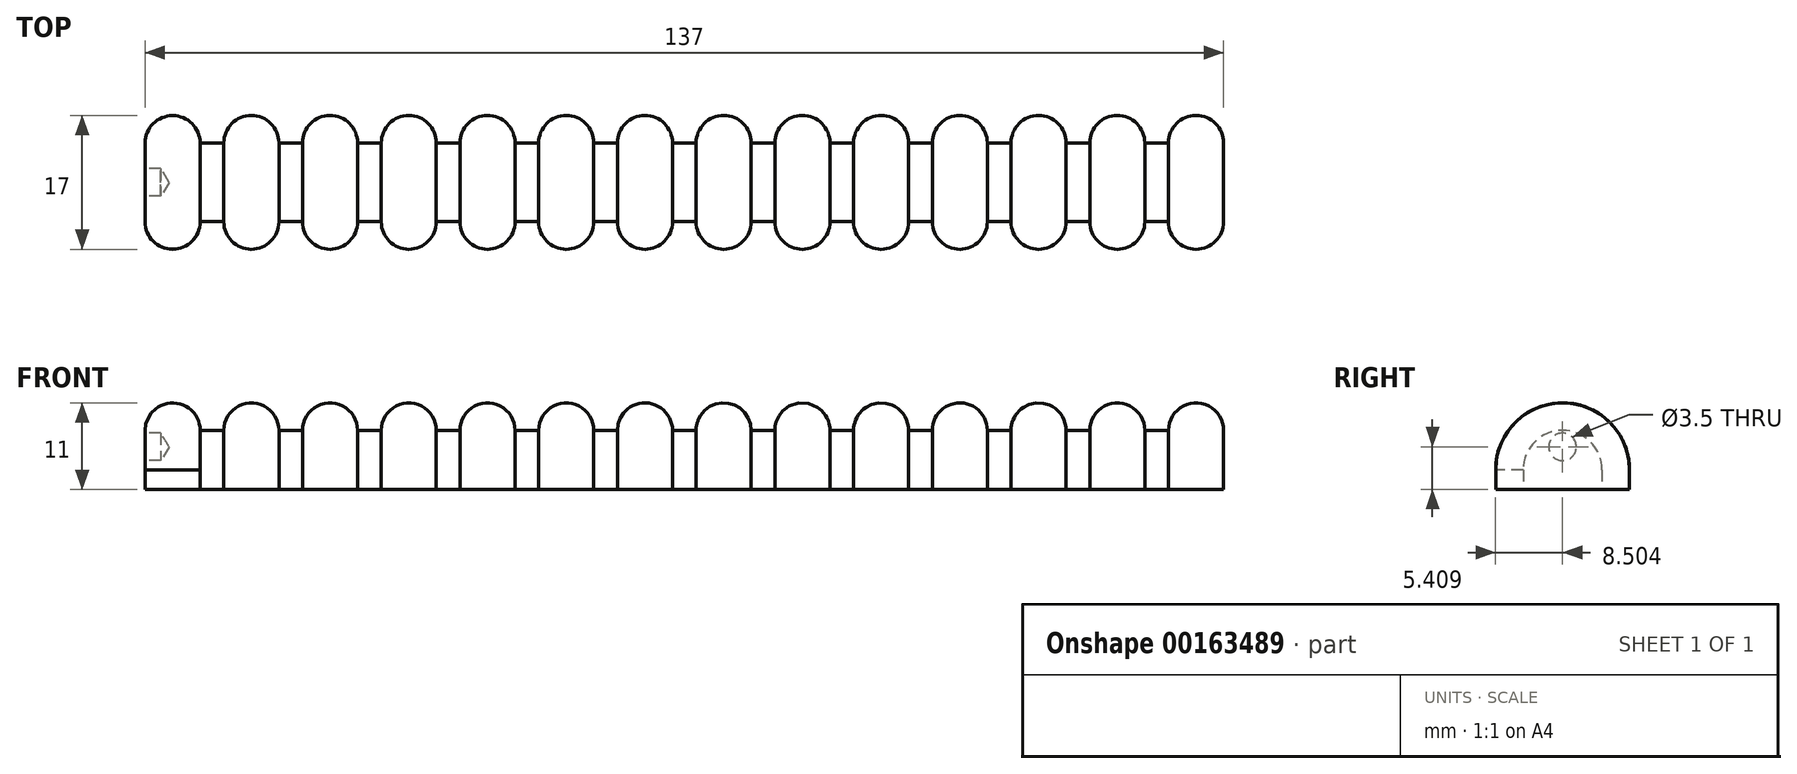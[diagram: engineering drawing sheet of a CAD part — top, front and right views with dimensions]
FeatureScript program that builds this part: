
annotation { "Feature Type Name" : "Feature", "Feature Type Description" : "" }
export const myFeature = defineFeature(function(context is Context, id is Id, definition is map)
    precondition{}
    {
        {
            var Q0;
            Q0=qCreatedBy(makeId("Top.planeOp"),FACE);
            var sketch = newSketch(context, id + "F0", { "sketchPlane" : qUnion([Q0])});
            skLineSegment(sketch, "E0", {"start": v(9.65, 1.22) * mm, "end": v(9.65, 0.22) * mm});
            skLineSegment(sketch, "E1", {"start": v(9.65, 0.22) * mm, "end": v(14.65, 0.22) * mm});
            skLineSegment(sketch, "E2", {"start": v(14.65, 0.22) * mm, "end": v(14.65, 1.22) * mm});
            skLineSegment(sketch, "E3", {"start": v(19.65, 1.22) * mm, "end": v(19.65, 0.22) * mm});
            skLineSegment(sketch, "E4", {"start": v(19.65, 0.22) * mm, "end": v(24.65, 0.22) * mm});
            skLineSegment(sketch, "E5", {"start": v(24.65, 0.22) * mm, "end": v(24.65, 1.22) * mm});
            skLineSegment(sketch, "E6", {"start": v(29.65, 1.22) * mm, "end": v(29.65, 0.22) * mm});
            skLineSegment(sketch, "E7", {"start": v(29.65, 0.22) * mm, "end": v(34.65, 0.22) * mm});
            skLineSegment(sketch, "E8", {"start": v(34.65, 0.22) * mm, "end": v(34.65, 1.22) * mm});
            skLineSegment(sketch, "E9", {"start": v(39.65, 1.22) * mm, "end": v(39.65, 0.22) * mm});
            skLineSegment(sketch, "E10", {"start": v(39.65, 0.22) * mm, "end": v(44.65, 0.22) * mm});
            skLineSegment(sketch, "E11", {"start": v(44.65, 0.22) * mm, "end": v(44.65, 1.22) * mm});
            skLineSegment(sketch, "E12", {"start": v(49.65, 1.22) * mm, "end": v(49.65, 0.22) * mm});
            skLineSegment(sketch, "E13", {"start": v(49.65, 0.22) * mm, "end": v(54.65, 0.22) * mm});
            skLineSegment(sketch, "E14", {"start": v(54.65, 0.22) * mm, "end": v(54.65, 1.22) * mm});
            skLineSegment(sketch, "E15", {"start": v(59.65, 1.22) * mm, "end": v(59.65, 0.22) * mm});
            skLineSegment(sketch, "E16", {"start": v(59.65, 0.22) * mm, "end": v(64.65, 0.22) * mm});
            skLineSegment(sketch, "E17", {"start": v(64.65, 0.22) * mm, "end": v(64.65, 1.22) * mm});
            skLineSegment(sketch, "E18", {"start": v(69.65, 1.22) * mm, "end": v(69.65, 0.22) * mm});
            skLineSegment(sketch, "E19", {"start": v(69.65, 0.22) * mm, "end": v(74.65, 0.22) * mm});
            skLineSegment(sketch, "E20", {"start": v(74.65, 0.22) * mm, "end": v(74.65, 1.22) * mm});
            skLineSegment(sketch, "E21", {"start": v(79.65, 1.22) * mm, "end": v(79.65, 0.22) * mm});
            skLineSegment(sketch, "E22", {"start": v(79.65, 0.22) * mm, "end": v(84.65, 0.22) * mm});
            skLineSegment(sketch, "E23", {"start": v(84.65, 0.22) * mm, "end": v(84.65, 1.22) * mm});
            skLineSegment(sketch, "E24", {"start": v(89.65, 1.22) * mm, "end": v(89.65, 0.22) * mm});
            skLineSegment(sketch, "E25", {"start": v(89.65, 0.22) * mm, "end": v(94.65, 0.22) * mm});
            skLineSegment(sketch, "E26", {"start": v(94.65, 0.22) * mm, "end": v(94.65, 1.22) * mm});
            skLineSegment(sketch, "E27", {"start": v(99.65, 1.22) * mm, "end": v(99.65, 0.22) * mm});
            skLineSegment(sketch, "E28", {"start": v(99.65, 0.22) * mm, "end": v(104.65, 0.22) * mm});
            skLineSegment(sketch, "E29", {"start": v(104.65, 0.22) * mm, "end": v(104.65, 1.22) * mm});
            skLineSegment(sketch, "E30", {"start": v(109.65, 1.22) * mm, "end": v(109.65, 0.22) * mm});
            skLineSegment(sketch, "E31", {"start": v(109.65, 0.22) * mm, "end": v(114.65, 0.22) * mm});
            skLineSegment(sketch, "E32", {"start": v(114.65, 0.22) * mm, "end": v(114.65, 1.22) * mm});
            skLineSegment(sketch, "E33", {"start": v(119.65, 1.22) * mm, "end": v(119.65, 0.22) * mm});
            skLineSegment(sketch, "E34", {"start": v(119.65, 0.22) * mm, "end": v(124.65, 0.22) * mm});
            skLineSegment(sketch, "E35", {"start": v(124.65, 0.22) * mm, "end": v(124.65, 1.22) * mm});
            skLineSegment(sketch, "E36", {"start": v(124.65, 1.22) * mm, "end": v(127.15, 1.22) * mm});
            skLineSegment(sketch, "E37", {"start": v(129.65, 1.22) * mm, "end": v(129.65, 0.22) * mm});
            skLineSegment(sketch, "E38", {"start": v(129.65, 0.22) * mm, "end": v(134.65, 0.22) * mm});
            skLineSegment(sketch, "E39", {"start": v(134.65, 0.22) * mm, "end": v(134.65, 1.22) * mm});
            skLineSegment(sketch, "E40", {"start": v(139.65, 1.22) * mm, "end": v(139.65, -8.78) * mm});
            skLineSegment(sketch, "E41", {"start": v(134.65, -8.78) * mm, "end": v(134.65, -7.78) * mm});
            skLineSegment(sketch, "E42", {"start": v(134.65, -7.78) * mm, "end": v(129.65, -7.78) * mm});
            skLineSegment(sketch, "E43", {"start": v(129.65, -7.78) * mm, "end": v(129.65, -8.78) * mm});
            skLineSegment(sketch, "E44", {"start": v(124.65, -8.78) * mm, "end": v(124.65, -7.78) * mm});
            skLineSegment(sketch, "E45", {"start": v(124.65, -7.78) * mm, "end": v(119.65, -7.78) * mm});
            skLineSegment(sketch, "E46", {"start": v(119.65, -7.78) * mm, "end": v(119.65, -8.78) * mm});
            skLineSegment(sketch, "E47", {"start": v(114.65, -8.78) * mm, "end": v(114.65, -7.78) * mm});
            skLineSegment(sketch, "E48", {"start": v(114.65, -7.78) * mm, "end": v(109.65, -7.78) * mm});
            skLineSegment(sketch, "E49", {"start": v(109.65, -7.78) * mm, "end": v(109.65, -8.78) * mm});
            skLineSegment(sketch, "E50", {"start": v(104.65, -8.78) * mm, "end": v(104.65, -7.78) * mm});
            skLineSegment(sketch, "E51", {"start": v(69.65, -7.78) * mm, "end": v(69.65, -8.78) * mm});
            skLineSegment(sketch, "E52", {"start": v(64.65, -8.78) * mm, "end": v(64.65, -7.78) * mm});
            skLineSegment(sketch, "E53", {"start": v(64.65, -7.78) * mm, "end": v(59.65, -7.78) * mm});
            skLineSegment(sketch, "E54", {"start": v(59.65, -7.78) * mm, "end": v(59.65, -8.78) * mm});
            skLineSegment(sketch, "E55", {"start": v(54.65, -8.78) * mm, "end": v(54.65, -7.78) * mm});
            skLineSegment(sketch, "E56", {"start": v(54.65, -7.78) * mm, "end": v(49.65, -7.78) * mm});
            skLineSegment(sketch, "E57", {"start": v(49.65, -7.78) * mm, "end": v(49.65, -8.78) * mm});
            skLineSegment(sketch, "E58", {"start": v(44.65, -8.78) * mm, "end": v(44.65, -7.78) * mm});
            skLineSegment(sketch, "E59", {"start": v(44.65, -7.78) * mm, "end": v(39.65, -7.78) * mm});
            skLineSegment(sketch, "E60", {"start": v(39.65, -7.78) * mm, "end": v(39.65, -8.78) * mm});
            skLineSegment(sketch, "E61", {"start": v(34.65, -8.78) * mm, "end": v(34.65, -7.78) * mm});
            skLineSegment(sketch, "E62", {"start": v(34.65, -7.78) * mm, "end": v(29.65, -7.78) * mm});
            skLineSegment(sketch, "E63", {"start": v(29.65, -7.78) * mm, "end": v(29.65, -8.78) * mm});
            skLineSegment(sketch, "E64", {"start": v(24.65, -8.78) * mm, "end": v(24.65, -7.78) * mm});
            skLineSegment(sketch, "E65", {"start": v(24.65, -7.78) * mm, "end": v(19.65, -7.78) * mm});
            skLineSegment(sketch, "E66", {"start": v(19.65, -7.78) * mm, "end": v(19.65, -8.78) * mm});
            skLineSegment(sketch, "E67", {"start": v(14.65, -8.78) * mm, "end": v(14.65, -7.78) * mm});
            skLineSegment(sketch, "E68", {"start": v(14.65, -7.78) * mm, "end": v(9.65, -7.78) * mm});
            skLineSegment(sketch, "E69", {"start": v(9.65, -7.78) * mm, "end": v(9.65, -8.78) * mm});
            skLineSegment(sketch, "E70", {"start": v(4.65, -8.78) * mm, "end": v(4.65, 1.22) * mm});
            skArc(sketch, "E71", {"start": v(4.65, 1.22) * mm, "mid": v(7.15, 3.7) * mm, "end": v(9.65, 1.22) * mm});
            skArc(sketch, "E72", {"start": v(14.65, 1.22) * mm, "mid": v(17.15, 3.72) * mm, "end": v(19.65, 1.22) * mm});
            skArc(sketch, "E73", {"start": v(4.65, -8.78) * mm, "mid": v(7.15, -11.28) * mm, "end": v(9.65, -8.78) * mm});
            skArc(sketch, "E74", {"start": v(14.65, -8.78) * mm, "mid": v(17.15, -11.28) * mm, "end": v(19.65, -8.78) * mm});
            skLineSegment(sketch, "E75", {"start": v(79.65, -7.78) * mm, "end": v(79.65, -8.78) * mm});
            skLineSegment(sketch, "E76", {"start": v(74.65, -8.78) * mm, "end": v(74.65, -7.78) * mm});
            skLineSegment(sketch, "E77", {"start": v(74.65, -7.78) * mm, "end": v(69.65, -7.78) * mm});
            skArc(sketch, "E78", {"start": v(24.65, -8.78) * mm, "mid": v(27.15, -11.28) * mm, "end": v(29.65, -8.78) * mm});
            skArc(sketch, "E79", {"start": v(24.65, 1.22) * mm, "mid": v(27.15, 3.72) * mm, "end": v(29.65, 1.22) * mm});
            skArc(sketch, "E80", {"start": v(34.65, 1.22) * mm, "mid": v(37.15, 3.72) * mm, "end": v(39.65, 1.22) * mm});
            skArc(sketch, "E81", {"start": v(34.65, -8.78) * mm, "mid": v(37.15, -11.28) * mm, "end": v(39.65, -8.78) * mm});
            skArc(sketch, "E82", {"start": v(44.65, -8.78) * mm, "mid": v(47.15, -11.28) * mm, "end": v(49.65, -8.78) * mm});
            skArc(sketch, "E83", {"start": v(44.65, 1.22) * mm, "mid": v(47.15, 3.72) * mm, "end": v(49.65, 1.22) * mm});
            skArc(sketch, "E84", {"start": v(54.65, 1.22) * mm, "mid": v(57.15, 3.72) * mm, "end": v(59.65, 1.22) * mm});
            skArc(sketch, "E85", {"start": v(54.65, -8.78) * mm, "mid": v(57.15, -11.28) * mm, "end": v(59.65, -8.78) * mm});
            skArc(sketch, "E86", {"start": v(64.65, -8.78) * mm, "mid": v(67.15, -11.28) * mm, "end": v(69.65, -8.78) * mm});
            skArc(sketch, "E87", {"start": v(64.65, 1.22) * mm, "mid": v(67.15, 3.72) * mm, "end": v(69.65, 1.22) * mm});
            skArc(sketch, "E88", {"start": v(74.65, 1.22) * mm, "mid": v(77.15, 3.72) * mm, "end": v(79.65, 1.22) * mm});
            skArc(sketch, "E89", {"start": v(74.65, -8.78) * mm, "mid": v(77.15, -11.28) * mm, "end": v(79.65, -8.78) * mm});
            skArc(sketch, "E90", {"start": v(84.65, 1.22) * mm, "mid": v(87.15, 3.72) * mm, "end": v(89.65, 1.22) * mm});
            skArc(sketch, "E91", {"start": v(104.65, -8.78) * mm, "mid": v(107.15, -11.28) * mm, "end": v(109.65, -8.78) * mm});
            skLineSegment(sketch, "E92", {"start": v(79.65, -7.78) * mm, "end": v(84.65, -7.78) * mm});
            skLineSegment(sketch, "E93", {"start": v(84.65, -7.78) * mm, "end": v(84.65, -8.78) * mm});
            skLineSegment(sketch, "E94", {"start": v(89.65, -8.78) * mm, "end": v(89.65, -7.78) * mm});
            skLineSegment(sketch, "E95", {"start": v(89.65, -7.78) * mm, "end": v(94.65, -7.78) * mm});
            skLineSegment(sketch, "E96", {"start": v(94.65, -7.78) * mm, "end": v(94.65, -8.78) * mm});
            skLineSegment(sketch, "E97", {"start": v(99.65, -8.78) * mm, "end": v(99.65, -7.78) * mm});
            skLineSegment(sketch, "E98", {"start": v(99.65, -7.78) * mm, "end": v(104.65, -7.78) * mm});
            skArc(sketch, "E99", {"start": v(84.65, -8.78) * mm, "mid": v(87.15, -11.28) * mm, "end": v(89.65, -8.78) * mm});
            skArc(sketch, "E100", {"start": v(94.65, -8.78) * mm, "mid": v(97.15, -11.28) * mm, "end": v(99.65, -8.78) * mm});
            skArc(sketch, "E101", {"start": v(94.65, 1.22) * mm, "mid": v(97.15, 3.72) * mm, "end": v(99.65, 1.22) * mm});
            skArc(sketch, "E102", {"start": v(104.65, 1.22) * mm, "mid": v(107.15, 3.72) * mm, "end": v(109.65, 1.22) * mm});
            skArc(sketch, "E103", {"start": v(114.65, 1.22) * mm, "mid": v(117.15, 3.72) * mm, "end": v(119.65, 1.22) * mm});
            skArc(sketch, "E104", {"start": v(114.65, -8.78) * mm, "mid": v(117.15, -11.28) * mm, "end": v(119.65, -8.78) * mm});
            skArc(sketch, "E105", {"start": v(124.65, 1.22) * mm, "mid": v(127.15, 3.72) * mm, "end": v(129.65, 1.22) * mm});
            skArc(sketch, "E106", {"start": v(134.65, 1.22) * mm, "mid": v(137.15, 3.72) * mm, "end": v(139.65, 1.22) * mm});
            skArc(sketch, "E107", {"start": v(134.65, -8.78) * mm, "mid": v(137.15, -11.28) * mm, "end": v(139.65, -8.78) * mm});
            skArc(sketch, "E108", {"start": v(124.65, -8.78) * mm, "mid": v(127.15, -11.28) * mm, "end": v(129.65, -8.78) * mm});
            skSolve(sketch);
        }
        {
            var Q0;
            Q0=makeQuery(id+"F0.imprint","IMPRINT",FACE,{"disambiguationData":[TD([[makeQuery(id+"F0.imprint","IMPRINT",EDGE,{"derivedFrom":sQuery(id+"F0.wireOp",EDGE,"E0")}),-1.0]])]});
            extrude(context, id + "F1", {"entities" : qUnion([Q0]), "depth" : 2.5 * mm});
        }
        {
            var Q0;
            Q0=qCreatedBy(makeId("Top.planeOp"),FACE);
            var sketch = newSketch(context, id + "F2", { "sketchPlane" : qUnion([Q0])});
            skLineSegment(sketch, "E109.0", {"start": v(4.65, -8.78) * mm, "end": v(4.65, 1.22) * mm});
            skArc(sketch, "E109.1", {"start": v(4.65, 1.22) * mm, "mid": v(7.15, 3.7) * mm, "end": v(9.65, 1.22) * mm});
            skLineSegment(sketch, "E109.2", {"start": v(9.65, 1.22) * mm, "end": v(9.65, 0.22) * mm});
            skLineSegment(sketch, "E109.3", {"start": v(9.65, 0.22) * mm, "end": v(14.65, 0.22) * mm});
            skArc(sketch, "E109.4", {"start": v(4.65, -8.78) * mm, "mid": v(7.15, -11.28) * mm, "end": v(9.65, -8.78) * mm});
            skLineSegment(sketch, "E109.5", {"start": v(9.65, -7.78) * mm, "end": v(9.65, -8.78) * mm});
            skLineSegment(sketch, "E109.6", {"start": v(14.65, -7.78) * mm, "end": v(9.65, -7.78) * mm});
            skLineSegment(sketch, "E109.7", {"start": v(14.65, -8.78) * mm, "end": v(14.65, -7.78) * mm});
            skArc(sketch, "E109.8", {"start": v(14.65, -8.78) * mm, "mid": v(17.15, -11.28) * mm, "end": v(19.65, -8.78) * mm});
            skLineSegment(sketch, "E109.9", {"start": v(19.65, -7.78) * mm, "end": v(19.65, -8.78) * mm});
            skLineSegment(sketch, "E109.10", {"start": v(24.65, -7.78) * mm, "end": v(19.65, -7.78) * mm});
            skLineSegment(sketch, "E109.11", {"start": v(19.65, 0.22) * mm, "end": v(24.65, 0.22) * mm});
            skLineSegment(sketch, "E109.12", {"start": v(19.65, 1.22) * mm, "end": v(19.65, 0.22) * mm});
            skArc(sketch, "E109.13", {"start": v(14.65, 1.22) * mm, "mid": v(17.15, 3.72) * mm, "end": v(19.65, 1.22) * mm});
            skLineSegment(sketch, "E109.14", {"start": v(14.65, 0.22) * mm, "end": v(14.65, 1.22) * mm});
            skLineSegment(sketch, "E109.15", {"start": v(24.65, 0.22) * mm, "end": v(24.65, 1.22) * mm});
            skArc(sketch, "E109.16", {"start": v(24.65, 1.22) * mm, "mid": v(27.15, 3.72) * mm, "end": v(29.65, 1.22) * mm});
            skLineSegment(sketch, "E109.17", {"start": v(29.65, 1.22) * mm, "end": v(29.65, 0.22) * mm});
            skLineSegment(sketch, "E109.18", {"start": v(29.65, 0.22) * mm, "end": v(34.65, 0.22) * mm});
            skLineSegment(sketch, "E109.19", {"start": v(24.65, -8.78) * mm, "end": v(24.65, -7.78) * mm});
            skArc(sketch, "E109.20", {"start": v(24.65, -8.78) * mm, "mid": v(27.15, -11.28) * mm, "end": v(29.65, -8.78) * mm});
            skLineSegment(sketch, "E109.21", {"start": v(29.65, -7.78) * mm, "end": v(29.65, -8.78) * mm});
            skLineSegment(sketch, "E109.22", {"start": v(34.65, -7.78) * mm, "end": v(29.65, -7.78) * mm});
            skArc(sketch, "E109.23", {"start": v(34.65, 1.22) * mm, "mid": v(37.15, 3.72) * mm, "end": v(39.65, 1.22) * mm});
            skLineSegment(sketch, "E109.24", {"start": v(34.65, 0.22) * mm, "end": v(34.65, 1.22) * mm});
            skLineSegment(sketch, "E109.25", {"start": v(39.65, 1.22) * mm, "end": v(39.65, 0.22) * mm});
            skLineSegment(sketch, "E109.26", {"start": v(44.65, 0.22) * mm, "end": v(44.65, 1.22) * mm});
            skArc(sketch, "E109.27", {"start": v(44.65, 1.22) * mm, "mid": v(47.15, 3.72) * mm, "end": v(49.65, 1.22) * mm});
            skLineSegment(sketch, "E109.28", {"start": v(49.65, 1.22) * mm, "end": v(49.65, 0.22) * mm});
            skLineSegment(sketch, "E109.29", {"start": v(49.65, 0.22) * mm, "end": v(54.65, 0.22) * mm});
            skLineSegment(sketch, "E109.30", {"start": v(39.65, 0.22) * mm, "end": v(44.65, 0.22) * mm});
            skLineSegment(sketch, "E109.31", {"start": v(34.65, -8.78) * mm, "end": v(34.65, -7.78) * mm});
            skArc(sketch, "E109.32", {"start": v(34.65, -8.78) * mm, "mid": v(37.15, -11.28) * mm, "end": v(39.65, -8.78) * mm});
            skLineSegment(sketch, "E109.33", {"start": v(39.65, -7.78) * mm, "end": v(39.65, -8.78) * mm});
            skLineSegment(sketch, "E109.34", {"start": v(44.65, -7.78) * mm, "end": v(39.65, -7.78) * mm});
            skLineSegment(sketch, "E109.35", {"start": v(44.65, -8.78) * mm, "end": v(44.65, -7.78) * mm});
            skArc(sketch, "E109.36", {"start": v(44.65, -8.78) * mm, "mid": v(47.15, -11.28) * mm, "end": v(49.65, -8.78) * mm});
            skLineSegment(sketch, "E109.37", {"start": v(49.65, -7.78) * mm, "end": v(49.65, -8.78) * mm});
            skLineSegment(sketch, "E109.38", {"start": v(54.65, -7.78) * mm, "end": v(49.65, -7.78) * mm});
            skLineSegment(sketch, "E109.39", {"start": v(54.65, 0.22) * mm, "end": v(54.65, 1.22) * mm});
            skArc(sketch, "E109.40", {"start": v(54.65, 1.22) * mm, "mid": v(57.15, 3.72) * mm, "end": v(59.65, 1.22) * mm});
            skLineSegment(sketch, "E109.41", {"start": v(59.65, 1.22) * mm, "end": v(59.65, 0.22) * mm});
            skLineSegment(sketch, "E109.42", {"start": v(59.65, 0.22) * mm, "end": v(64.65, 0.22) * mm});
            skLineSegment(sketch, "E109.43", {"start": v(64.65, 0.22) * mm, "end": v(64.65, 1.22) * mm});
            skArc(sketch, "E109.44", {"start": v(64.65, 1.22) * mm, "mid": v(67.15, 3.72) * mm, "end": v(69.65, 1.22) * mm});
            skLineSegment(sketch, "E109.45", {"start": v(69.65, 1.22) * mm, "end": v(69.65, 0.22) * mm});
            skLineSegment(sketch, "E109.46", {"start": v(69.65, 0.22) * mm, "end": v(74.65, 0.22) * mm});
            skLineSegment(sketch, "E109.47", {"start": v(74.65, 0.22) * mm, "end": v(74.65, 1.22) * mm});
            skArc(sketch, "E109.48", {"start": v(74.65, 1.22) * mm, "mid": v(77.15, 3.72) * mm, "end": v(79.65, 1.22) * mm});
            skLineSegment(sketch, "E109.49", {"start": v(79.65, 1.22) * mm, "end": v(79.65, 0.22) * mm});
            skLineSegment(sketch, "E109.50", {"start": v(79.65, 0.22) * mm, "end": v(84.65, 0.22) * mm});
            skLineSegment(sketch, "E109.51", {"start": v(64.65, -7.78) * mm, "end": v(59.65, -7.78) * mm});
            skLineSegment(sketch, "E109.52", {"start": v(59.65, -7.78) * mm, "end": v(59.65, -8.78) * mm});
            skArc(sketch, "E109.53", {"start": v(54.65, -8.78) * mm, "mid": v(57.15, -11.28) * mm, "end": v(59.65, -8.78) * mm});
            skLineSegment(sketch, "E109.54", {"start": v(54.65, -8.78) * mm, "end": v(54.65, -7.78) * mm});
            skLineSegment(sketch, "E110.0", {"start": v(64.65, -8.78) * mm, "end": v(64.65, -7.78) * mm});
            skArc(sketch, "E110.1", {"start": v(64.65, -8.78) * mm, "mid": v(67.15, -11.28) * mm, "end": v(69.65, -8.78) * mm});
            skLineSegment(sketch, "E110.2", {"start": v(69.65, -7.78) * mm, "end": v(69.65, -8.78) * mm});
            skLineSegment(sketch, "E110.3", {"start": v(74.65, -7.78) * mm, "end": v(69.65, -7.78) * mm});
            skLineSegment(sketch, "E110.4", {"start": v(74.65, -8.78) * mm, "end": v(74.65, -7.78) * mm});
            skArc(sketch, "E110.5", {"start": v(74.65, -8.78) * mm, "mid": v(77.15, -11.28) * mm, "end": v(79.65, -8.78) * mm});
            skLineSegment(sketch, "E110.6", {"start": v(79.65, -7.78) * mm, "end": v(79.65, -8.78) * mm});
            skLineSegment(sketch, "E110.7", {"start": v(79.65, -7.78) * mm, "end": v(84.65, -7.78) * mm});
            skLineSegment(sketch, "E110.8", {"start": v(84.65, 0.22) * mm, "end": v(84.65, 1.22) * mm});
            skArc(sketch, "E110.9", {"start": v(84.65, 1.22) * mm, "mid": v(87.15, 3.72) * mm, "end": v(89.65, 1.22) * mm});
            skLineSegment(sketch, "E110.10", {"start": v(89.65, 1.22) * mm, "end": v(89.65, 0.22) * mm});
            skLineSegment(sketch, "E110.11", {"start": v(89.65, 0.22) * mm, "end": v(94.65, 0.22) * mm});
            skLineSegment(sketch, "E110.12", {"start": v(94.65, 0.22) * mm, "end": v(94.65, 1.22) * mm});
            skArc(sketch, "E110.13", {"start": v(94.65, 1.22) * mm, "mid": v(97.15, 3.72) * mm, "end": v(99.65, 1.22) * mm});
            skLineSegment(sketch, "E110.14", {"start": v(99.65, 1.22) * mm, "end": v(99.65, 0.22) * mm});
            skLineSegment(sketch, "E110.15", {"start": v(99.65, 0.22) * mm, "end": v(104.65, 0.22) * mm});
            skLineSegment(sketch, "E110.16", {"start": v(99.65, -7.78) * mm, "end": v(104.65, -7.78) * mm});
            skLineSegment(sketch, "E110.17", {"start": v(99.65, -8.78) * mm, "end": v(99.65, -7.78) * mm});
            skArc(sketch, "E110.18", {"start": v(94.65, -8.78) * mm, "mid": v(97.15, -11.28) * mm, "end": v(99.65, -8.78) * mm});
            skLineSegment(sketch, "E110.19", {"start": v(94.65, -7.78) * mm, "end": v(94.65, -8.78) * mm});
            skLineSegment(sketch, "E110.20", {"start": v(89.65, -7.78) * mm, "end": v(94.65, -7.78) * mm});
            skLineSegment(sketch, "E110.21", {"start": v(89.65, -8.78) * mm, "end": v(89.65, -7.78) * mm});
            skArc(sketch, "E110.22", {"start": v(84.65, -8.78) * mm, "mid": v(87.15, -11.28) * mm, "end": v(89.65, -8.78) * mm});
            skLineSegment(sketch, "E110.23", {"start": v(84.65, -7.78) * mm, "end": v(84.65, -8.78) * mm});
            skLineSegment(sketch, "E111.0", {"start": v(104.65, 0.22) * mm, "end": v(104.65, 1.22) * mm});
            skArc(sketch, "E111.1", {"start": v(104.65, 1.22) * mm, "mid": v(107.15, 3.72) * mm, "end": v(109.65, 1.22) * mm});
            skLineSegment(sketch, "E111.2", {"start": v(109.65, 1.22) * mm, "end": v(109.65, 0.22) * mm});
            skLineSegment(sketch, "E111.3", {"start": v(109.65, 0.22) * mm, "end": v(114.65, 0.22) * mm});
            skArc(sketch, "E111.4", {"start": v(114.65, 1.22) * mm, "mid": v(117.15, 3.72) * mm, "end": v(119.65, 1.22) * mm});
            skLineSegment(sketch, "E111.5", {"start": v(114.65, 0.22) * mm, "end": v(114.65, 1.22) * mm});
            skLineSegment(sketch, "E111.6", {"start": v(119.65, 1.22) * mm, "end": v(119.65, 0.22) * mm});
            skLineSegment(sketch, "E111.7", {"start": v(119.65, 0.22) * mm, "end": v(124.65, 0.22) * mm});
            skLineSegment(sketch, "E111.8", {"start": v(124.65, -7.78) * mm, "end": v(119.65, -7.78) * mm});
            skLineSegment(sketch, "E111.9", {"start": v(119.65, -7.78) * mm, "end": v(119.65, -8.78) * mm});
            skLineSegment(sketch, "E111.10", {"start": v(104.65, -8.78) * mm, "end": v(104.65, -7.78) * mm});
            skArc(sketch, "E111.11", {"start": v(104.65, -8.78) * mm, "mid": v(107.15, -11.28) * mm, "end": v(109.65, -8.78) * mm});
            skLineSegment(sketch, "E111.12", {"start": v(109.65, -7.78) * mm, "end": v(109.65, -8.78) * mm});
            skLineSegment(sketch, "E111.13", {"start": v(114.65, -7.78) * mm, "end": v(109.65, -7.78) * mm});
            skLineSegment(sketch, "E111.14", {"start": v(114.65, -8.78) * mm, "end": v(114.65, -7.78) * mm});
            skArc(sketch, "E111.15", {"start": v(114.65, -8.78) * mm, "mid": v(117.15, -11.28) * mm, "end": v(119.65, -8.78) * mm});
            skLineSegment(sketch, "E111.16", {"start": v(124.65, 0.22) * mm, "end": v(124.65, 1.22) * mm});
            skArc(sketch, "E111.17", {"start": v(124.65, 1.22) * mm, "mid": v(127.15, 3.72) * mm, "end": v(129.65, 1.22) * mm});
            skLineSegment(sketch, "E111.18", {"start": v(129.65, 1.22) * mm, "end": v(129.65, 0.22) * mm});
            skLineSegment(sketch, "E111.19", {"start": v(129.65, 0.22) * mm, "end": v(134.65, 0.22) * mm});
            skLineSegment(sketch, "E111.20", {"start": v(134.65, 0.22) * mm, "end": v(134.65, 1.22) * mm});
            skArc(sketch, "E111.21", {"start": v(134.65, 1.22) * mm, "mid": v(137.15, 3.72) * mm, "end": v(139.65, 1.22) * mm});
            skLineSegment(sketch, "E111.22", {"start": v(139.65, 1.22) * mm, "end": v(139.65, -8.78) * mm});
            skArc(sketch, "E111.23", {"start": v(134.65, -8.78) * mm, "mid": v(137.15, -11.28) * mm, "end": v(139.65, -8.78) * mm});
            skLineSegment(sketch, "E111.24", {"start": v(134.65, -8.78) * mm, "end": v(134.65, -7.78) * mm});
            skLineSegment(sketch, "E111.25", {"start": v(134.65, -7.78) * mm, "end": v(129.65, -7.78) * mm});
            skLineSegment(sketch, "E111.26", {"start": v(129.65, -7.78) * mm, "end": v(129.65, -8.78) * mm});
            skArc(sketch, "E111.27", {"start": v(124.65, -8.78) * mm, "mid": v(127.15, -11.28) * mm, "end": v(129.65, -8.78) * mm});
            skLineSegment(sketch, "E111.28", {"start": v(124.65, -8.78) * mm, "end": v(124.65, -7.78) * mm});
            skLineSegment(sketch, "E112.0", {"start": v(113.65, -8.78) * mm, "end": v(113.65, -8.78) * mm});
            skLineSegment(sketch, "E112.1", {"start": v(113.65, -8.78) * mm, "end": v(110.65, -8.78) * mm});
            skLineSegment(sketch, "E112.2", {"start": v(110.65, -8.78) * mm, "end": v(110.65, -8.78) * mm});
            skArc(sketch, "E112.3", {"start": v(103.65, -8.78) * mm, "mid": v(107.15, -12.28) * mm, "end": v(110.65, -8.78) * mm});
            skLineSegment(sketch, "E112.4", {"start": v(103.65, -8.78) * mm, "end": v(103.65, -8.78) * mm});
            skLineSegment(sketch, "E112.5", {"start": v(100.65, -8.78) * mm, "end": v(103.65, -8.78) * mm});
            skLineSegment(sketch, "E112.6", {"start": v(100.65, -8.78) * mm, "end": v(100.65, -8.78) * mm});
            skArc(sketch, "E112.7", {"start": v(93.65, -8.78) * mm, "mid": v(97.15, -12.28) * mm, "end": v(100.65, -8.78) * mm});
            skLineSegment(sketch, "E112.8", {"start": v(93.65, -8.78) * mm, "end": v(93.65, -8.78) * mm});
            skLineSegment(sketch, "E112.9", {"start": v(90.65, -8.78) * mm, "end": v(93.65, -8.78) * mm});
            skLineSegment(sketch, "E112.10", {"start": v(90.65, -8.78) * mm, "end": v(90.65, -8.78) * mm});
            skArc(sketch, "E112.11", {"start": v(43.65, 1.22) * mm, "mid": v(47.15, 4.72) * mm, "end": v(50.65, 1.22) * mm});
            skLineSegment(sketch, "E112.12", {"start": v(50.65, 1.22) * mm, "end": v(50.65, 1.22) * mm});
            skLineSegment(sketch, "E112.13", {"start": v(50.65, 1.22) * mm, "end": v(53.65, 1.22) * mm});
            skLineSegment(sketch, "E112.14", {"start": v(53.65, 1.22) * mm, "end": v(53.65, 1.22) * mm});
            skArc(sketch, "E112.15", {"start": v(53.65, 1.22) * mm, "mid": v(57.15, 4.72) * mm, "end": v(60.65, 1.22) * mm});
            skLineSegment(sketch, "E112.16", {"start": v(60.65, 1.22) * mm, "end": v(60.65, 1.22) * mm});
            skLineSegment(sketch, "E112.17", {"start": v(60.65, 1.22) * mm, "end": v(63.65, 1.22) * mm});
            skLineSegment(sketch, "E112.18", {"start": v(63.65, 1.22) * mm, "end": v(63.65, 1.22) * mm});
            skArc(sketch, "E112.19", {"start": v(63.65, 1.22) * mm, "mid": v(67.15, 4.72) * mm, "end": v(70.65, 1.22) * mm});
            skLineSegment(sketch, "E112.20", {"start": v(70.65, 1.22) * mm, "end": v(70.65, 1.22) * mm});
            skLineSegment(sketch, "E112.21", {"start": v(70.65, 1.22) * mm, "end": v(73.65, 1.22) * mm});
            skLineSegment(sketch, "E112.22", {"start": v(73.65, 1.22) * mm, "end": v(73.65, 1.22) * mm});
            skArc(sketch, "E112.23", {"start": v(73.65, 1.22) * mm, "mid": v(77.15, 4.72) * mm, "end": v(80.65, 1.22) * mm});
            skLineSegment(sketch, "E112.24", {"start": v(80.65, 1.22) * mm, "end": v(80.65, 1.22) * mm});
            skLineSegment(sketch, "E112.25", {"start": v(80.65, 1.22) * mm, "end": v(83.65, 1.22) * mm});
            skLineSegment(sketch, "E112.26", {"start": v(83.65, 1.22) * mm, "end": v(83.65, 1.22) * mm});
            skArc(sketch, "E112.27", {"start": v(83.65, 1.22) * mm, "mid": v(87.15, 4.72) * mm, "end": v(90.65, 1.22) * mm});
            skLineSegment(sketch, "E112.28", {"start": v(90.65, 1.22) * mm, "end": v(90.65, 1.22) * mm});
            skLineSegment(sketch, "E112.29", {"start": v(90.65, 1.22) * mm, "end": v(93.65, 1.22) * mm});
            skLineSegment(sketch, "E112.30", {"start": v(93.65, 1.22) * mm, "end": v(93.65, 1.22) * mm});
            skArc(sketch, "E112.31", {"start": v(93.65, 1.22) * mm, "mid": v(97.15, 4.72) * mm, "end": v(100.65, 1.22) * mm});
            skLineSegment(sketch, "E112.32", {"start": v(100.65, 1.22) * mm, "end": v(100.65, 1.22) * mm});
            skLineSegment(sketch, "E112.33", {"start": v(100.65, 1.22) * mm, "end": v(103.65, 1.22) * mm});
            skLineSegment(sketch, "E112.34", {"start": v(103.65, 1.22) * mm, "end": v(103.65, 1.22) * mm});
            skArc(sketch, "E112.35", {"start": v(133.65, 1.22) * mm, "mid": v(137.15, 4.72) * mm, "end": v(140.65, 1.22) * mm});
            skLineSegment(sketch, "E112.36", {"start": v(140.65, 1.22) * mm, "end": v(140.65, -8.78) * mm});
            skArc(sketch, "E112.37", {"start": v(133.65, -8.78) * mm, "mid": v(137.15, -12.28) * mm, "end": v(140.65, -8.78) * mm});
            skLineSegment(sketch, "E112.38", {"start": v(133.65, -8.78) * mm, "end": v(133.65, -8.78) * mm});
            skLineSegment(sketch, "E112.39", {"start": v(133.65, -8.78) * mm, "end": v(130.65, -8.78) * mm});
            skLineSegment(sketch, "E112.40", {"start": v(130.65, -8.78) * mm, "end": v(130.65, -8.78) * mm});
            skLineSegment(sketch, "E112.41", {"start": v(120.65, -8.78) * mm, "end": v(120.65, -8.78) * mm});
            skLineSegment(sketch, "E112.42", {"start": v(123.65, -8.78) * mm, "end": v(120.65, -8.78) * mm});
            skLineSegment(sketch, "E112.43", {"start": v(123.65, -8.78) * mm, "end": v(123.65, -8.78) * mm});
            skArc(sketch, "E112.44", {"start": v(123.65, -8.78) * mm, "mid": v(127.15, -12.28) * mm, "end": v(130.65, -8.78) * mm});
            skLineSegment(sketch, "E112.45", {"start": v(133.65, 1.22) * mm, "end": v(133.65, 1.22) * mm});
            skLineSegment(sketch, "E112.46", {"start": v(130.65, 1.22) * mm, "end": v(133.65, 1.22) * mm});
            skLineSegment(sketch, "E112.47", {"start": v(130.65, 1.22) * mm, "end": v(130.65, 1.22) * mm});
            skArc(sketch, "E112.48", {"start": v(123.65, 1.22) * mm, "mid": v(127.15, 4.72) * mm, "end": v(130.65, 1.22) * mm});
            skLineSegment(sketch, "E112.49", {"start": v(123.65, 1.22) * mm, "end": v(123.65, 1.22) * mm});
            skLineSegment(sketch, "E112.50", {"start": v(120.65, 1.22) * mm, "end": v(123.65, 1.22) * mm});
            skLineSegment(sketch, "E112.51", {"start": v(120.65, 1.22) * mm, "end": v(120.65, 1.22) * mm});
            skArc(sketch, "E112.52", {"start": v(113.65, 1.22) * mm, "mid": v(117.15, 4.72) * mm, "end": v(120.65, 1.22) * mm});
            skLineSegment(sketch, "E112.53", {"start": v(113.65, 1.22) * mm, "end": v(113.65, 1.22) * mm});
            skLineSegment(sketch, "E112.54", {"start": v(110.65, 1.22) * mm, "end": v(113.65, 1.22) * mm});
            skLineSegment(sketch, "E112.55", {"start": v(110.65, 1.22) * mm, "end": v(110.65, 1.22) * mm});
            skArc(sketch, "E112.56", {"start": v(103.65, 1.22) * mm, "mid": v(107.15, 4.72) * mm, "end": v(110.65, 1.22) * mm});
            skLineSegment(sketch, "E112.57", {"start": v(43.65, 1.22) * mm, "end": v(43.65, 1.22) * mm});
            skLineSegment(sketch, "E112.58", {"start": v(40.65, 1.22) * mm, "end": v(43.65, 1.22) * mm});
            skLineSegment(sketch, "E112.59", {"start": v(40.65, 1.22) * mm, "end": v(40.65, 1.22) * mm});
            skArc(sketch, "E112.60", {"start": v(33.65, 1.22) * mm, "mid": v(37.15, 4.72) * mm, "end": v(40.65, 1.22) * mm});
            skLineSegment(sketch, "E112.61", {"start": v(33.65, 1.22) * mm, "end": v(33.65, 1.22) * mm});
            skLineSegment(sketch, "E112.62", {"start": v(30.65, 1.22) * mm, "end": v(33.65, 1.22) * mm});
            skLineSegment(sketch, "E112.63", {"start": v(30.65, 1.22) * mm, "end": v(30.65, 1.22) * mm});
            skArc(sketch, "E112.64", {"start": v(23.65, 1.22) * mm, "mid": v(27.15, 4.72) * mm, "end": v(30.65, 1.22) * mm});
            skLineSegment(sketch, "E112.65", {"start": v(23.65, 1.22) * mm, "end": v(23.65, 1.22) * mm});
            skLineSegment(sketch, "E112.66", {"start": v(20.65, 1.22) * mm, "end": v(23.65, 1.22) * mm});
            skLineSegment(sketch, "E112.67", {"start": v(20.65, 1.22) * mm, "end": v(20.65, 1.22) * mm});
            skArc(sketch, "E112.68", {"start": v(113.65, -8.78) * mm, "mid": v(117.15, -12.28) * mm, "end": v(120.65, -8.78) * mm});
            skArc(sketch, "E112.69", {"start": v(13.65, 1.22) * mm, "mid": v(17.15, 4.72) * mm, "end": v(20.65, 1.22) * mm});
            skLineSegment(sketch, "E112.70", {"start": v(13.65, 1.22) * mm, "end": v(13.65, 1.22) * mm});
            skLineSegment(sketch, "E112.71", {"start": v(10.65, 1.22) * mm, "end": v(13.65, 1.22) * mm});
            skLineSegment(sketch, "E112.72", {"start": v(10.65, 1.23) * mm, "end": v(10.65, 1.22) * mm});
            skArc(sketch, "E112.73", {"start": v(3.65, 1.23) * mm, "mid": v(7.15, 4.7) * mm, "end": v(10.65, 1.23) * mm});
            skLineSegment(sketch, "E112.74", {"start": v(3.65, -8.78) * mm, "end": v(3.65, 1.23) * mm});
            skArc(sketch, "E112.75", {"start": v(3.65, -8.78) * mm, "mid": v(7.15, -12.28) * mm, "end": v(10.65, -8.78) * mm});
            skLineSegment(sketch, "E112.76", {"start": v(10.65, -8.78) * mm, "end": v(10.65, -8.78) * mm});
            skLineSegment(sketch, "E112.77", {"start": v(13.65, -8.78) * mm, "end": v(10.65, -8.78) * mm});
            skLineSegment(sketch, "E112.78", {"start": v(13.65, -8.78) * mm, "end": v(13.65, -8.78) * mm});
            skArc(sketch, "E112.79", {"start": v(13.65, -8.78) * mm, "mid": v(17.15, -12.28) * mm, "end": v(20.65, -8.78) * mm});
            skLineSegment(sketch, "E112.80", {"start": v(20.65, -8.78) * mm, "end": v(20.65, -8.78) * mm});
            skLineSegment(sketch, "E112.81", {"start": v(23.65, -8.78) * mm, "end": v(20.65, -8.78) * mm});
            skLineSegment(sketch, "E112.82", {"start": v(23.65, -8.78) * mm, "end": v(23.65, -8.78) * mm});
            skArc(sketch, "E112.83", {"start": v(23.65, -8.78) * mm, "mid": v(27.15, -12.28) * mm, "end": v(30.65, -8.78) * mm});
            skLineSegment(sketch, "E112.84", {"start": v(30.65, -8.78) * mm, "end": v(30.65, -8.78) * mm});
            skLineSegment(sketch, "E112.85", {"start": v(33.65, -8.78) * mm, "end": v(30.65, -8.78) * mm});
            skLineSegment(sketch, "E112.86", {"start": v(33.65, -8.78) * mm, "end": v(33.65, -8.78) * mm});
            skArc(sketch, "E112.87", {"start": v(33.65, -8.78) * mm, "mid": v(37.15, -12.28) * mm, "end": v(40.65, -8.78) * mm});
            skLineSegment(sketch, "E112.88", {"start": v(40.65, -8.78) * mm, "end": v(40.65, -8.78) * mm});
            skLineSegment(sketch, "E112.89", {"start": v(43.65, -8.78) * mm, "end": v(40.65, -8.78) * mm});
            skLineSegment(sketch, "E112.90", {"start": v(43.65, -8.78) * mm, "end": v(43.65, -8.78) * mm});
            skArc(sketch, "E112.91", {"start": v(43.65, -8.78) * mm, "mid": v(47.15, -12.28) * mm, "end": v(50.65, -8.78) * mm});
            skLineSegment(sketch, "E112.92", {"start": v(50.65, -8.78) * mm, "end": v(50.65, -8.78) * mm});
            skLineSegment(sketch, "E112.93", {"start": v(53.65, -8.78) * mm, "end": v(50.65, -8.78) * mm});
            skLineSegment(sketch, "E112.94", {"start": v(53.65, -8.78) * mm, "end": v(53.65, -8.78) * mm});
            skArc(sketch, "E112.95", {"start": v(53.65, -8.78) * mm, "mid": v(57.15, -12.28) * mm, "end": v(60.65, -8.78) * mm});
            skLineSegment(sketch, "E112.96", {"start": v(60.65, -8.78) * mm, "end": v(60.65, -8.78) * mm});
            skLineSegment(sketch, "E112.97", {"start": v(63.65, -8.78) * mm, "end": v(60.65, -8.78) * mm});
            skLineSegment(sketch, "E112.98", {"start": v(63.65, -8.78) * mm, "end": v(63.65, -8.78) * mm});
            skArc(sketch, "E112.99", {"start": v(63.65, -8.78) * mm, "mid": v(67.15, -12.28) * mm, "end": v(70.65, -8.78) * mm});
            skLineSegment(sketch, "E112.100", {"start": v(70.65, -8.78) * mm, "end": v(70.65, -8.78) * mm});
            skLineSegment(sketch, "E112.101", {"start": v(73.65, -8.78) * mm, "end": v(70.65, -8.78) * mm});
            skLineSegment(sketch, "E112.102", {"start": v(73.65, -8.78) * mm, "end": v(73.65, -8.78) * mm});
            skArc(sketch, "E112.103", {"start": v(73.65, -8.78) * mm, "mid": v(77.15, -12.28) * mm, "end": v(80.65, -8.78) * mm});
            skLineSegment(sketch, "E112.104", {"start": v(80.65, -8.78) * mm, "end": v(80.65, -8.78) * mm});
            skLineSegment(sketch, "E112.105", {"start": v(80.65, -8.78) * mm, "end": v(83.65, -8.78) * mm});
            skLineSegment(sketch, "E112.106", {"start": v(83.65, -8.78) * mm, "end": v(83.65, -8.78) * mm});
            skArc(sketch, "E112.107", {"start": v(83.65, -8.78) * mm, "mid": v(87.15, -12.28) * mm, "end": v(90.65, -8.78) * mm});
            skSolve(sketch);
        }
        {
            var Q0;
            Q0=makeQuery(id+"F1.opExtrude","CAP_FACE",FACE,{"disambiguationData":[OSD([sQuery(id+"F0.wireOp",EDGE,"E0"),sQuery(id+"F0.wireOp",EDGE,"E1"),sQuery(id+"F0.wireOp",EDGE,"E2"),sQuery(id+"F0.wireOp",EDGE,"E3"),sQuery(id+"F0.wireOp",EDGE,"E4"),sQuery(id+"F0.wireOp",EDGE,"E5"),sQuery(id+"F0.wireOp",EDGE,"E6"),sQuery(id+"F0.wireOp",EDGE,"E7"),sQuery(id+"F0.wireOp",EDGE,"E8"),sQuery(id+"F0.wireOp",EDGE,"E9"),sQuery(id+"F0.wireOp",EDGE,"E10"),sQuery(id+"F0.wireOp",EDGE,"E11"),sQuery(id+"F0.wireOp",EDGE,"E12"),sQuery(id+"F0.wireOp",EDGE,"E13"),sQuery(id+"F0.wireOp",EDGE,"E14"),sQuery(id+"F0.wireOp",EDGE,"E15"),sQuery(id+"F0.wireOp",EDGE,"E16"),sQuery(id+"F0.wireOp",EDGE,"E17"),sQuery(id+"F0.wireOp",EDGE,"E18"),sQuery(id+"F0.wireOp",EDGE,"E19"),sQuery(id+"F0.wireOp",EDGE,"E20"),sQuery(id+"F0.wireOp",EDGE,"E21"),sQuery(id+"F0.wireOp",EDGE,"E22"),sQuery(id+"F0.wireOp",EDGE,"E23"),sQuery(id+"F0.wireOp",EDGE,"E24"),sQuery(id+"F0.wireOp",EDGE,"E25"),sQuery(id+"F0.wireOp",EDGE,"E26"),sQuery(id+"F0.wireOp",EDGE,"E27"),sQuery(id+"F0.wireOp",EDGE,"E28"),sQuery(id+"F0.wireOp",EDGE,"E29"),sQuery(id+"F0.wireOp",EDGE,"E30"),sQuery(id+"F0.wireOp",EDGE,"E31"),sQuery(id+"F0.wireOp",EDGE,"E32"),sQuery(id+"F0.wireOp",EDGE,"E33"),sQuery(id+"F0.wireOp",EDGE,"E34"),sQuery(id+"F0.wireOp",EDGE,"E35"),sQuery(id+"F0.wireOp",EDGE,"E37"),sQuery(id+"F0.wireOp",EDGE,"E38"),sQuery(id+"F0.wireOp",EDGE,"E39"),sQuery(id+"F0.wireOp",EDGE,"E40"),sQuery(id+"F0.wireOp",EDGE,"E41"),sQuery(id+"F0.wireOp",EDGE,"E42"),sQuery(id+"F0.wireOp",EDGE,"E43"),sQuery(id+"F0.wireOp",EDGE,"E44"),sQuery(id+"F0.wireOp",EDGE,"E45"),sQuery(id+"F0.wireOp",EDGE,"E46"),sQuery(id+"F0.wireOp",EDGE,"E47"),sQuery(id+"F0.wireOp",EDGE,"E48"),sQuery(id+"F0.wireOp",EDGE,"E49"),sQuery(id+"F0.wireOp",EDGE,"E50"),sQuery(id+"F0.wireOp",EDGE,"E51"),sQuery(id+"F0.wireOp",EDGE,"E52"),sQuery(id+"F0.wireOp",EDGE,"E53"),sQuery(id+"F0.wireOp",EDGE,"E54"),sQuery(id+"F0.wireOp",EDGE,"E55"),sQuery(id+"F0.wireOp",EDGE,"E56"),sQuery(id+"F0.wireOp",EDGE,"E57"),sQuery(id+"F0.wireOp",EDGE,"E58"),sQuery(id+"F0.wireOp",EDGE,"E59"),sQuery(id+"F0.wireOp",EDGE,"E60"),sQuery(id+"F0.wireOp",EDGE,"E61"),sQuery(id+"F0.wireOp",EDGE,"E62"),sQuery(id+"F0.wireOp",EDGE,"E63"),sQuery(id+"F0.wireOp",EDGE,"E64"),sQuery(id+"F0.wireOp",EDGE,"E65"),sQuery(id+"F0.wireOp",EDGE,"E66"),sQuery(id+"F0.wireOp",EDGE,"E67"),sQuery(id+"F0.wireOp",EDGE,"E68"),sQuery(id+"F0.wireOp",EDGE,"E69"),sQuery(id+"F0.wireOp",EDGE,"E70"),sQuery(id+"F0.wireOp",EDGE,"E71"),sQuery(id+"F0.wireOp",EDGE,"E72"),sQuery(id+"F0.wireOp",EDGE,"E73"),sQuery(id+"F0.wireOp",EDGE,"E74"),sQuery(id+"F0.wireOp",EDGE,"E75"),sQuery(id+"F0.wireOp",EDGE,"E76"),sQuery(id+"F0.wireOp",EDGE,"E77"),sQuery(id+"F0.wireOp",EDGE,"E78"),sQuery(id+"F0.wireOp",EDGE,"E79"),sQuery(id+"F0.wireOp",EDGE,"E80"),sQuery(id+"F0.wireOp",EDGE,"E81"),sQuery(id+"F0.wireOp",EDGE,"E82"),sQuery(id+"F0.wireOp",EDGE,"E83"),sQuery(id+"F0.wireOp",EDGE,"E84"),sQuery(id+"F0.wireOp",EDGE,"E85"),sQuery(id+"F0.wireOp",EDGE,"E86"),sQuery(id+"F0.wireOp",EDGE,"E87"),sQuery(id+"F0.wireOp",EDGE,"E88"),sQuery(id+"F0.wireOp",EDGE,"E89"),sQuery(id+"F0.wireOp",EDGE,"E90"),sQuery(id+"F0.wireOp",EDGE,"E91"),sQuery(id+"F0.wireOp",EDGE,"E92"),sQuery(id+"F0.wireOp",EDGE,"E93"),sQuery(id+"F0.wireOp",EDGE,"E94"),sQuery(id+"F0.wireOp",EDGE,"E95"),sQuery(id+"F0.wireOp",EDGE,"E96"),sQuery(id+"F0.wireOp",EDGE,"E97"),sQuery(id+"F0.wireOp",EDGE,"E98"),sQuery(id+"F0.wireOp",EDGE,"E99"),sQuery(id+"F0.wireOp",EDGE,"E100"),sQuery(id+"F0.wireOp",EDGE,"E101"),sQuery(id+"F0.wireOp",EDGE,"E102"),sQuery(id+"F0.wireOp",EDGE,"E103"),sQuery(id+"F0.wireOp",EDGE,"E104"),sQuery(id+"F0.wireOp",EDGE,"E105"),sQuery(id+"F0.wireOp",EDGE,"E106"),sQuery(id+"F0.wireOp",EDGE,"E107"),sQuery(id+"F0.wireOp",EDGE,"E108")])],"isStart":false});
            var sketch = newSketch(context, id + "F3", { "sketchPlane" : qUnion([Q0])});
            skArc(sketch, "E113.0", {"start": v(4.65, 1.22) * mm, "mid": v(7.15, 3.7) * mm, "end": v(9.65, 1.22) * mm});
            skLineSegment(sketch, "E113.1", {"start": v(9.65, 1.22) * mm, "end": v(9.65, 0.22) * mm});
            skLineSegment(sketch, "E113.2", {"start": v(9.65, 0.22) * mm, "end": v(14.65, 0.22) * mm});
            skLineSegment(sketch, "E113.3", {"start": v(14.65, 0.22) * mm, "end": v(14.65, 1.22) * mm});
            skArc(sketch, "E113.4", {"start": v(14.65, 1.22) * mm, "mid": v(17.15, 3.72) * mm, "end": v(19.65, 1.22) * mm});
            skLineSegment(sketch, "E113.5", {"start": v(19.65, 1.22) * mm, "end": v(19.65, 0.22) * mm});
            skLineSegment(sketch, "E113.6", {"start": v(19.65, 0.22) * mm, "end": v(24.65, 0.22) * mm});
            skLineSegment(sketch, "E113.7", {"start": v(24.65, 0.22) * mm, "end": v(24.65, 1.22) * mm});
            skArc(sketch, "E113.8", {"start": v(24.65, 1.22) * mm, "mid": v(27.15, 3.72) * mm, "end": v(29.65, 1.22) * mm});
            skLineSegment(sketch, "E113.9", {"start": v(29.65, 1.22) * mm, "end": v(29.65, 0.22) * mm});
            skLineSegment(sketch, "E113.10", {"start": v(29.65, 0.22) * mm, "end": v(34.65, 0.22) * mm});
            skLineSegment(sketch, "E113.11", {"start": v(34.65, 0.22) * mm, "end": v(34.65, 1.22) * mm});
            skArc(sketch, "E113.12", {"start": v(34.65, 1.22) * mm, "mid": v(37.15, 3.72) * mm, "end": v(39.65, 1.22) * mm});
            skLineSegment(sketch, "E113.13", {"start": v(39.65, 1.22) * mm, "end": v(39.65, 0.22) * mm});
            skLineSegment(sketch, "E113.14", {"start": v(39.65, 0.22) * mm, "end": v(44.65, 0.22) * mm});
            skLineSegment(sketch, "E113.15", {"start": v(44.65, 0.22) * mm, "end": v(44.65, 1.22) * mm});
            skArc(sketch, "E113.16", {"start": v(44.65, 1.22) * mm, "mid": v(47.15, 3.72) * mm, "end": v(49.65, 1.22) * mm});
            skLineSegment(sketch, "E113.17", {"start": v(49.65, 1.22) * mm, "end": v(49.65, 0.22) * mm});
            skLineSegment(sketch, "E113.18", {"start": v(49.65, 0.22) * mm, "end": v(54.65, 0.22) * mm});
            skLineSegment(sketch, "E113.19", {"start": v(54.65, 0.22) * mm, "end": v(54.65, 1.22) * mm});
            skArc(sketch, "E113.20", {"start": v(54.65, 1.22) * mm, "mid": v(57.15, 3.72) * mm, "end": v(59.65, 1.22) * mm});
            skLineSegment(sketch, "E113.21", {"start": v(59.65, 1.22) * mm, "end": v(59.65, 0.22) * mm});
            skLineSegment(sketch, "E113.22", {"start": v(59.65, 0.22) * mm, "end": v(64.65, 0.22) * mm});
            skLineSegment(sketch, "E113.23", {"start": v(64.65, 0.22) * mm, "end": v(64.65, 1.22) * mm});
            skArc(sketch, "E113.24", {"start": v(64.65, 1.22) * mm, "mid": v(67.15, 3.72) * mm, "end": v(69.65, 1.22) * mm});
            skLineSegment(sketch, "E113.25", {"start": v(69.65, 1.22) * mm, "end": v(69.65, 0.22) * mm});
            skLineSegment(sketch, "E113.26", {"start": v(69.65, 0.22) * mm, "end": v(74.65, 0.22) * mm});
            skLineSegment(sketch, "E113.27", {"start": v(74.65, 0.22) * mm, "end": v(74.65, 1.22) * mm});
            skArc(sketch, "E113.28", {"start": v(74.65, 1.22) * mm, "mid": v(77.15, 3.72) * mm, "end": v(79.65, 1.22) * mm});
            skLineSegment(sketch, "E113.29", {"start": v(79.65, 1.22) * mm, "end": v(79.65, 0.22) * mm});
            skLineSegment(sketch, "E113.30", {"start": v(79.65, 0.22) * mm, "end": v(84.65, 0.22) * mm});
            skLineSegment(sketch, "E113.31", {"start": v(84.65, 0.22) * mm, "end": v(84.65, 1.22) * mm});
            skArc(sketch, "E113.32", {"start": v(84.65, 1.22) * mm, "mid": v(87.15, 3.72) * mm, "end": v(89.65, 1.22) * mm});
            skLineSegment(sketch, "E113.33", {"start": v(89.65, 1.22) * mm, "end": v(89.65, 0.22) * mm});
            skLineSegment(sketch, "E113.34", {"start": v(89.65, 0.22) * mm, "end": v(94.65, 0.22) * mm});
            skLineSegment(sketch, "E113.35", {"start": v(94.65, 0.22) * mm, "end": v(94.65, 1.22) * mm});
            skArc(sketch, "E113.36", {"start": v(94.65, 1.22) * mm, "mid": v(97.15, 3.72) * mm, "end": v(99.65, 1.22) * mm});
            skLineSegment(sketch, "E113.37", {"start": v(99.65, 1.22) * mm, "end": v(99.65, 0.22) * mm});
            skLineSegment(sketch, "E113.38", {"start": v(99.65, 0.22) * mm, "end": v(104.65, 0.22) * mm});
            skLineSegment(sketch, "E113.39", {"start": v(104.65, 0.22) * mm, "end": v(104.65, 1.22) * mm});
            skArc(sketch, "E113.40", {"start": v(104.65, 1.22) * mm, "mid": v(107.15, 3.72) * mm, "end": v(109.65, 1.22) * mm});
            skLineSegment(sketch, "E113.41", {"start": v(109.65, 1.22) * mm, "end": v(109.65, 0.22) * mm});
            skLineSegment(sketch, "E113.42", {"start": v(109.65, 0.22) * mm, "end": v(114.65, 0.22) * mm});
            skLineSegment(sketch, "E113.43", {"start": v(114.65, 0.22) * mm, "end": v(114.65, 1.22) * mm});
            skArc(sketch, "E113.44", {"start": v(114.65, 1.22) * mm, "mid": v(117.15, 3.72) * mm, "end": v(119.65, 1.22) * mm});
            skLineSegment(sketch, "E113.45", {"start": v(119.65, 1.22) * mm, "end": v(119.65, 0.22) * mm});
            skLineSegment(sketch, "E113.46", {"start": v(119.65, 0.22) * mm, "end": v(124.65, 0.22) * mm});
            skLineSegment(sketch, "E113.47", {"start": v(124.65, 0.22) * mm, "end": v(124.65, 1.22) * mm});
            skArc(sketch, "E113.48", {"start": v(124.65, 1.22) * mm, "mid": v(127.15, 3.72) * mm, "end": v(129.65, 1.22) * mm});
            skLineSegment(sketch, "E113.49", {"start": v(129.65, 1.22) * mm, "end": v(129.65, 0.22) * mm});
            skLineSegment(sketch, "E113.50", {"start": v(129.65, 0.22) * mm, "end": v(134.65, 0.22) * mm});
            skLineSegment(sketch, "E113.51", {"start": v(134.65, 0.22) * mm, "end": v(134.65, 1.22) * mm});
            skArc(sketch, "E113.52", {"start": v(134.65, 1.22) * mm, "mid": v(137.15, 3.72) * mm, "end": v(139.65, 1.22) * mm});
            skLineSegment(sketch, "E114", {"start": v(139.65, 1.22) * mm, "end": v(139.65, -3.78) * mm});
            skLineSegment(sketch, "E115", {"start": v(4.65, 1.22) * mm, "end": v(4.65, -3.78) * mm});
            skLineSegment(sketch, "E116.0", {"start": v(140.65, 1.22) * mm, "end": v(140.65, -3.78) * mm});
            skArc(sketch, "E116.1", {"start": v(133.65, 1.22) * mm, "mid": v(137.15, 4.72) * mm, "end": v(140.65, 1.22) * mm});
            skLineSegment(sketch, "E116.2", {"start": v(130.65, 1.22) * mm, "end": v(133.65, 1.22) * mm});
            skArc(sketch, "E116.3", {"start": v(123.65, 1.22) * mm, "mid": v(127.15, 4.72) * mm, "end": v(130.65, 1.22) * mm});
            skLineSegment(sketch, "E116.4", {"start": v(120.65, 1.22) * mm, "end": v(123.65, 1.22) * mm});
            skArc(sketch, "E116.5", {"start": v(113.65, 1.22) * mm, "mid": v(117.15, 4.72) * mm, "end": v(120.65, 1.22) * mm});
            skLineSegment(sketch, "E116.6", {"start": v(110.65, 1.22) * mm, "end": v(113.65, 1.22) * mm});
            skArc(sketch, "E116.7", {"start": v(43.65, 1.22) * mm, "mid": v(47.15, 4.72) * mm, "end": v(50.65, 1.22) * mm});
            skLineSegment(sketch, "E116.8", {"start": v(40.65, 1.22) * mm, "end": v(43.65, 1.22) * mm});
            skArc(sketch, "E116.9", {"start": v(33.65, 1.22) * mm, "mid": v(37.15, 4.72) * mm, "end": v(40.65, 1.22) * mm});
            skLineSegment(sketch, "E116.10", {"start": v(30.65, 1.22) * mm, "end": v(33.65, 1.22) * mm});
            skArc(sketch, "E116.11", {"start": v(23.65, 1.22) * mm, "mid": v(27.15, 4.72) * mm, "end": v(30.65, 1.22) * mm});
            skLineSegment(sketch, "E116.12", {"start": v(20.65, 1.22) * mm, "end": v(23.65, 1.22) * mm});
            skLineSegment(sketch, "E116.13", {"start": v(3.65, 1.23) * mm, "end": v(3.65, -3.78) * mm});
            skArc(sketch, "E116.14", {"start": v(3.65, 1.23) * mm, "mid": v(7.16, 4.7) * mm, "end": v(10.65, 1.22) * mm});
            skLineSegment(sketch, "E116.15", {"start": v(10.65, 1.22) * mm, "end": v(13.65, 1.22) * mm});
            skArc(sketch, "E116.16", {"start": v(13.65, 1.22) * mm, "mid": v(17.15, 4.72) * mm, "end": v(20.65, 1.22) * mm});
            skLineSegment(sketch, "E116.17", {"start": v(50.65, 1.22) * mm, "end": v(53.65, 1.22) * mm});
            skArc(sketch, "E116.18", {"start": v(53.65, 1.22) * mm, "mid": v(57.15, 4.72) * mm, "end": v(60.65, 1.22) * mm});
            skLineSegment(sketch, "E116.19", {"start": v(60.65, 1.22) * mm, "end": v(63.65, 1.22) * mm});
            skArc(sketch, "E116.20", {"start": v(63.65, 1.22) * mm, "mid": v(67.15, 4.72) * mm, "end": v(70.65, 1.22) * mm});
            skLineSegment(sketch, "E116.21", {"start": v(70.65, 1.22) * mm, "end": v(73.65, 1.22) * mm});
            skArc(sketch, "E116.22", {"start": v(73.65, 1.22) * mm, "mid": v(77.15, 4.72) * mm, "end": v(80.65, 1.22) * mm});
            skLineSegment(sketch, "E116.23", {"start": v(80.65, 1.22) * mm, "end": v(83.65, 1.22) * mm});
            skArc(sketch, "E116.24", {"start": v(83.65, 1.22) * mm, "mid": v(87.15, 4.72) * mm, "end": v(90.65, 1.22) * mm});
            skLineSegment(sketch, "E116.25", {"start": v(90.65, 1.22) * mm, "end": v(93.65, 1.22) * mm});
            skArc(sketch, "E116.26", {"start": v(93.65, 1.22) * mm, "mid": v(97.15, 4.72) * mm, "end": v(100.65, 1.22) * mm});
            skLineSegment(sketch, "E116.27", {"start": v(100.65, 1.22) * mm, "end": v(103.65, 1.22) * mm});
            skArc(sketch, "E116.28", {"start": v(103.65, 1.22) * mm, "mid": v(107.15, 4.72) * mm, "end": v(110.65, 1.22) * mm});
            skLineSegment(sketch, "E117", {"start": v(140.65, -3.78) * mm, "end": v(139.65, -3.78) * mm});
            skLineSegment(sketch, "E118", {"start": v(4.65, -3.78) * mm, "end": v(3.65, -3.78) * mm});
            skLineSegment(sketch, "E119", {"start": v(4.65, -3.78) * mm, "end": v(139.65, -3.78) * mm});
            skSolve(sketch);
        }
        {
            var Q0;
            Q0 = qSketchRegion(id + "F2", true);
            extrude(context, id + "F4", {"entities" : qUnion([Q0]), "operationType" : NewBodyOperationType.ADD, "depth" : 2.5 * mm});
        }
        {
            var Q0;
            Q0 = qSketchRegion(id + "F3", true);
            var Q1;
            Q1=sQuery(id+"F3.wireOp",EDGE,"E119");
            revolve(context, id + "F5", {"operationType" : NewBodyOperationType.ADD, "entities" : qUnion([Q0]), "axis" : qUnion([Q1]), "revolveType" : RevolveType.ONE_DIRECTION, "angle" : 180 * degree});
        }
        {
            var Q0;
            Q0=makeQuery(id+"F5.opRevolve","SWEPT_FACE",FACE,{"disambiguationData":[OSD([sQuery(id+"F3.wireOp",EDGE,"E116.13")])]});
            var sketch = newSketch(context, id + "F6", { "sketchPlane" : qUnion([Q0])});
            skPoint(sketch, "E120", {"position": v(3.78, 5.4) * mm});
            skPoint(sketch, "E120.positionSnap0", {"position": v(3.78, 2.5) * mm});
            skSolve(sketch);
        }
        {
            var Q0;
            Q0=sQuery(id+"F6.wireOp",VERTEX,"E120");
            var Q1;
            Q1=makeQuery(id+"F5.boolean.opBoolean","MERGE",BODY,{"derivedFrom":[makeQuery(id+"F1.opExtrude","SWEPT_BODY",BODY,{"disambiguationData":[OSD([sQuery(id+"F0.wireOp",EDGE,"E0"),sQuery(id+"F0.wireOp",EDGE,"E1"),sQuery(id+"F0.wireOp",EDGE,"E2"),sQuery(id+"F0.wireOp",EDGE,"E3"),sQuery(id+"F0.wireOp",EDGE,"E4"),sQuery(id+"F0.wireOp",EDGE,"E5"),sQuery(id+"F0.wireOp",EDGE,"E6"),sQuery(id+"F0.wireOp",EDGE,"E7"),sQuery(id+"F0.wireOp",EDGE,"E8"),sQuery(id+"F0.wireOp",EDGE,"E9"),sQuery(id+"F0.wireOp",EDGE,"E10"),sQuery(id+"F0.wireOp",EDGE,"E11"),sQuery(id+"F0.wireOp",EDGE,"E12"),sQuery(id+"F0.wireOp",EDGE,"E13"),sQuery(id+"F0.wireOp",EDGE,"E14"),sQuery(id+"F0.wireOp",EDGE,"E15"),sQuery(id+"F0.wireOp",EDGE,"E16"),sQuery(id+"F0.wireOp",EDGE,"E17"),sQuery(id+"F0.wireOp",EDGE,"E18"),sQuery(id+"F0.wireOp",EDGE,"E19"),sQuery(id+"F0.wireOp",EDGE,"E20"),sQuery(id+"F0.wireOp",EDGE,"E21"),sQuery(id+"F0.wireOp",EDGE,"E22"),sQuery(id+"F0.wireOp",EDGE,"E23"),sQuery(id+"F0.wireOp",EDGE,"E24"),sQuery(id+"F0.wireOp",EDGE,"E25"),sQuery(id+"F0.wireOp",EDGE,"E26"),sQuery(id+"F0.wireOp",EDGE,"E27"),sQuery(id+"F0.wireOp",EDGE,"E28"),sQuery(id+"F0.wireOp",EDGE,"E29"),sQuery(id+"F0.wireOp",EDGE,"E30"),sQuery(id+"F0.wireOp",EDGE,"E31"),sQuery(id+"F0.wireOp",EDGE,"E32"),sQuery(id+"F0.wireOp",EDGE,"E33"),sQuery(id+"F0.wireOp",EDGE,"E34"),sQuery(id+"F0.wireOp",EDGE,"E35"),sQuery(id+"F0.wireOp",EDGE,"E37"),sQuery(id+"F0.wireOp",EDGE,"E38"),sQuery(id+"F0.wireOp",EDGE,"E39"),sQuery(id+"F0.wireOp",EDGE,"E40"),sQuery(id+"F0.wireOp",EDGE,"E41"),sQuery(id+"F0.wireOp",EDGE,"E42"),sQuery(id+"F0.wireOp",EDGE,"E43"),sQuery(id+"F0.wireOp",EDGE,"E44"),sQuery(id+"F0.wireOp",EDGE,"E45"),sQuery(id+"F0.wireOp",EDGE,"E46"),sQuery(id+"F0.wireOp",EDGE,"E47"),sQuery(id+"F0.wireOp",EDGE,"E48"),sQuery(id+"F0.wireOp",EDGE,"E49"),sQuery(id+"F0.wireOp",EDGE,"E50"),sQuery(id+"F0.wireOp",EDGE,"E51"),sQuery(id+"F0.wireOp",EDGE,"E52"),sQuery(id+"F0.wireOp",EDGE,"E53"),sQuery(id+"F0.wireOp",EDGE,"E54"),sQuery(id+"F0.wireOp",EDGE,"E55"),sQuery(id+"F0.wireOp",EDGE,"E56"),sQuery(id+"F0.wireOp",EDGE,"E57"),sQuery(id+"F0.wireOp",EDGE,"E58"),sQuery(id+"F0.wireOp",EDGE,"E59"),sQuery(id+"F0.wireOp",EDGE,"E60"),sQuery(id+"F0.wireOp",EDGE,"E61"),sQuery(id+"F0.wireOp",EDGE,"E62"),sQuery(id+"F0.wireOp",EDGE,"E63"),sQuery(id+"F0.wireOp",EDGE,"E64"),sQuery(id+"F0.wireOp",EDGE,"E65"),sQuery(id+"F0.wireOp",EDGE,"E66"),sQuery(id+"F0.wireOp",EDGE,"E67"),sQuery(id+"F0.wireOp",EDGE,"E68"),sQuery(id+"F0.wireOp",EDGE,"E69"),sQuery(id+"F0.wireOp",EDGE,"E70"),sQuery(id+"F0.wireOp",EDGE,"E71"),sQuery(id+"F0.wireOp",EDGE,"E72"),sQuery(id+"F0.wireOp",EDGE,"E73"),sQuery(id+"F0.wireOp",EDGE,"E74"),sQuery(id+"F0.wireOp",EDGE,"E75"),sQuery(id+"F0.wireOp",EDGE,"E76"),sQuery(id+"F0.wireOp",EDGE,"E77"),sQuery(id+"F0.wireOp",EDGE,"E78"),sQuery(id+"F0.wireOp",EDGE,"E79"),sQuery(id+"F0.wireOp",EDGE,"E80"),sQuery(id+"F0.wireOp",EDGE,"E81"),sQuery(id+"F0.wireOp",EDGE,"E82"),sQuery(id+"F0.wireOp",EDGE,"E83"),sQuery(id+"F0.wireOp",EDGE,"E84"),sQuery(id+"F0.wireOp",EDGE,"E85"),sQuery(id+"F0.wireOp",EDGE,"E86"),sQuery(id+"F0.wireOp",EDGE,"E87"),sQuery(id+"F0.wireOp",EDGE,"E88"),sQuery(id+"F0.wireOp",EDGE,"E89"),sQuery(id+"F0.wireOp",EDGE,"E90"),sQuery(id+"F0.wireOp",EDGE,"E91"),sQuery(id+"F0.wireOp",EDGE,"E92"),sQuery(id+"F0.wireOp",EDGE,"E93"),sQuery(id+"F0.wireOp",EDGE,"E94"),sQuery(id+"F0.wireOp",EDGE,"E95"),sQuery(id+"F0.wireOp",EDGE,"E96"),sQuery(id+"F0.wireOp",EDGE,"E97"),sQuery(id+"F0.wireOp",EDGE,"E98"),sQuery(id+"F0.wireOp",EDGE,"E99"),sQuery(id+"F0.wireOp",EDGE,"E100"),sQuery(id+"F0.wireOp",EDGE,"E101"),sQuery(id+"F0.wireOp",EDGE,"E102"),sQuery(id+"F0.wireOp",EDGE,"E103"),sQuery(id+"F0.wireOp",EDGE,"E104"),sQuery(id+"F0.wireOp",EDGE,"E105"),sQuery(id+"F0.wireOp",EDGE,"E106"),sQuery(id+"F0.wireOp",EDGE,"E107"),sQuery(id+"F0.wireOp",EDGE,"E108")])]}),makeQuery(id+"F5.opRevolve","SWEPT_BODY",BODY,{"disambiguationData":[OSD([sQuery(id+"F3.wireOp",EDGE,"E116.0"),sQuery(id+"F3.wireOp",EDGE,"E116.1"),sQuery(id+"F3.wireOp",EDGE,"E116.2"),sQuery(id+"F3.wireOp",EDGE,"E116.3"),sQuery(id+"F3.wireOp",EDGE,"E116.4"),sQuery(id+"F3.wireOp",EDGE,"E116.5"),sQuery(id+"F3.wireOp",EDGE,"E116.6"),sQuery(id+"F3.wireOp",EDGE,"E116.7"),sQuery(id+"F3.wireOp",EDGE,"E116.8"),sQuery(id+"F3.wireOp",EDGE,"E116.9"),sQuery(id+"F3.wireOp",EDGE,"E116.10"),sQuery(id+"F3.wireOp",EDGE,"E116.11"),sQuery(id+"F3.wireOp",EDGE,"E116.12"),sQuery(id+"F3.wireOp",EDGE,"E116.13"),sQuery(id+"F3.wireOp",EDGE,"E116.14"),sQuery(id+"F3.wireOp",EDGE,"E116.15"),sQuery(id+"F3.wireOp",EDGE,"E116.16"),sQuery(id+"F3.wireOp",EDGE,"E116.17"),sQuery(id+"F3.wireOp",EDGE,"E116.18"),sQuery(id+"F3.wireOp",EDGE,"E116.19"),sQuery(id+"F3.wireOp",EDGE,"E116.20"),sQuery(id+"F3.wireOp",EDGE,"E116.21"),sQuery(id+"F3.wireOp",EDGE,"E116.22"),sQuery(id+"F3.wireOp",EDGE,"E116.23"),sQuery(id+"F3.wireOp",EDGE,"E116.24"),sQuery(id+"F3.wireOp",EDGE,"E116.25"),sQuery(id+"F3.wireOp",EDGE,"E116.26"),sQuery(id+"F3.wireOp",EDGE,"E116.27"),sQuery(id+"F3.wireOp",EDGE,"E116.28"),sQuery(id+"F3.wireOp",EDGE,"E117"),sQuery(id+"F3.wireOp",EDGE,"E118"),sQuery(id+"F3.wireOp",EDGE,"E119")])]})]});
            hole(context, id + "F7", {"style" : HoleStyle.SIMPLE, "endStyle" : HoleEndStyle.BLIND, "holeDiameter" : 3.5 * mm, "holeDepth" : 2 * mm, "locations" : qUnion([Q0]), "scope" : qUnion([Q1])});
        }
    });
